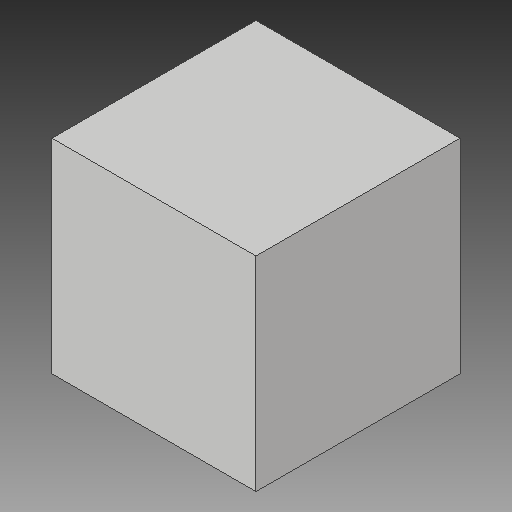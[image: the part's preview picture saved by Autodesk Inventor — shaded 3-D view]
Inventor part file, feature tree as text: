
AUTODESK INVENTOR PART (.ipt)
format: ipt  version: 2019 (Build 230136000, 136)  size: 83,456 bytes
history: native  units: in
note: dims shown in document units (in); Inventor stores cm internally (conversion verified against a paired STEP export)
features: extrude x1, sketch x1
ambient origin geometry x8: Origin, YZ Plane, XZ Plane, XY Plane, X Axis, Y Axis, Z Axis, Center Point
bodies: Solid1 (feature_tree)
feature tree (2):
  extrude  "Extrusion1"  Depth=6.0in
  sketch  "Sketch1"  dims[d0=6.0in d1=6.0in d2=6.0in d3=0.0in]
